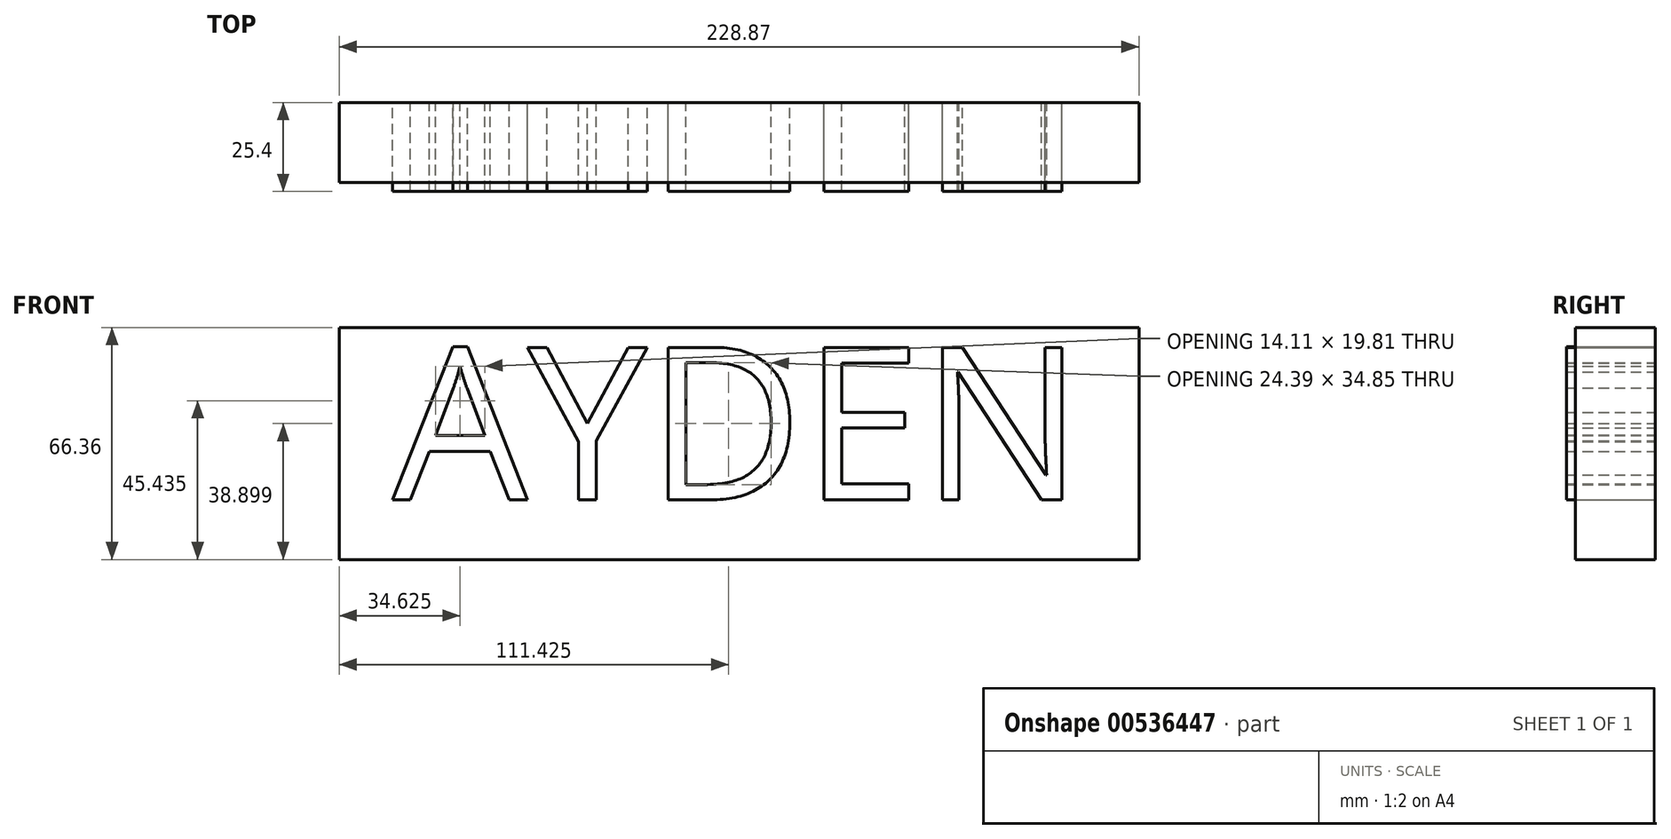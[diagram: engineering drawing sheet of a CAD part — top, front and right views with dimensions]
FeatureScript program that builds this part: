
annotation { "Feature Type Name" : "Feature", "Feature Type Description" : "" }
export const myFeature = defineFeature(function(context is Context, id is Id, definition is map)
    precondition{}
    {
        {
            var Q0;
            Q0=qCreatedBy(makeId("Front.planeOp"),FACE);
            var sketch = newSketch(context, id + "F0", { "sketchPlane" : qUnion([Q0])});
            skText(sketch, "E0", { "text": "AYDEN", "fontName": "OpenSans-Regular.ttf"});
            const initialGuessF0  = {"E0": [-0.12647, -0.044, 1, 0, 0.044]};
            skSetInitialGuess(sketch, initialGuessF0);
            skSolve(sketch);
        }
        {
            var Q0;
            Q0 = qSketchRegion(id + "F0", true);
            extrude(context, id + "F1", {"entities" : qUnion([Q0]), "depth" : 25.4 * mm, "offsetDistance" : 25.4 * mm});
        }
        {
            var Q0;
            Q0=qCreatedBy(makeId("Front.planeOp"),FACE);
            var sketch = newSketch(context, id + "F2", { "sketchPlane" : qUnion([Q0])});
            skLineSegment(sketch, "E1.bottom", {"start": v(-122.82, 11.16) * mm, "end": v(-144.22, 11.16) * mm});
            skLineSegment(sketch, "E1.top", {"start": v(-122.82, 11.16) * mm, "end": v(-144.22, 11.16) * mm});
            skLineSegment(sketch, "E1.left", {"start": v(-122.82, 11.16) * mm, "end": v(-122.82, 11.16) * mm});
            skLineSegment(sketch, "E1.right", {"start": v(-144.22, 11.16) * mm, "end": v(-144.22, 11.16) * mm});
            skLineSegment(sketch, "E2.bottom", {"start": v(-141.74, 5.27) * mm, "end": v(87.13, 5.27) * mm});
            skLineSegment(sketch, "E2.top", {"start": v(-141.74, -61.1) * mm, "end": v(87.13, -61.1) * mm});
            skLineSegment(sketch, "E2.left", {"start": v(-141.74, 5.27) * mm, "end": v(-141.74, -61.1) * mm});
            skLineSegment(sketch, "E2.right", {"start": v(87.13, 5.27) * mm, "end": v(87.13, -61.1) * mm});
            skSolve(sketch);
        }
        {
            var Q0;
            Q0=makeQuery(id+"F2.imprint","IMPRINT",FACE,{"disambiguationData":[TD([[makeQuery(id+"F2.imprint","IMPRINT",EDGE,{"derivedFrom":sQuery(id+"F2.wireOp",EDGE,"E2.bottom")}),-1.0]])]});
            extrude(context, id + "F3", {"entities" : qUnion([Q0]), "depth" : 22.86 * mm, "offsetDistance" : 25.4 * mm});
        }
    });
